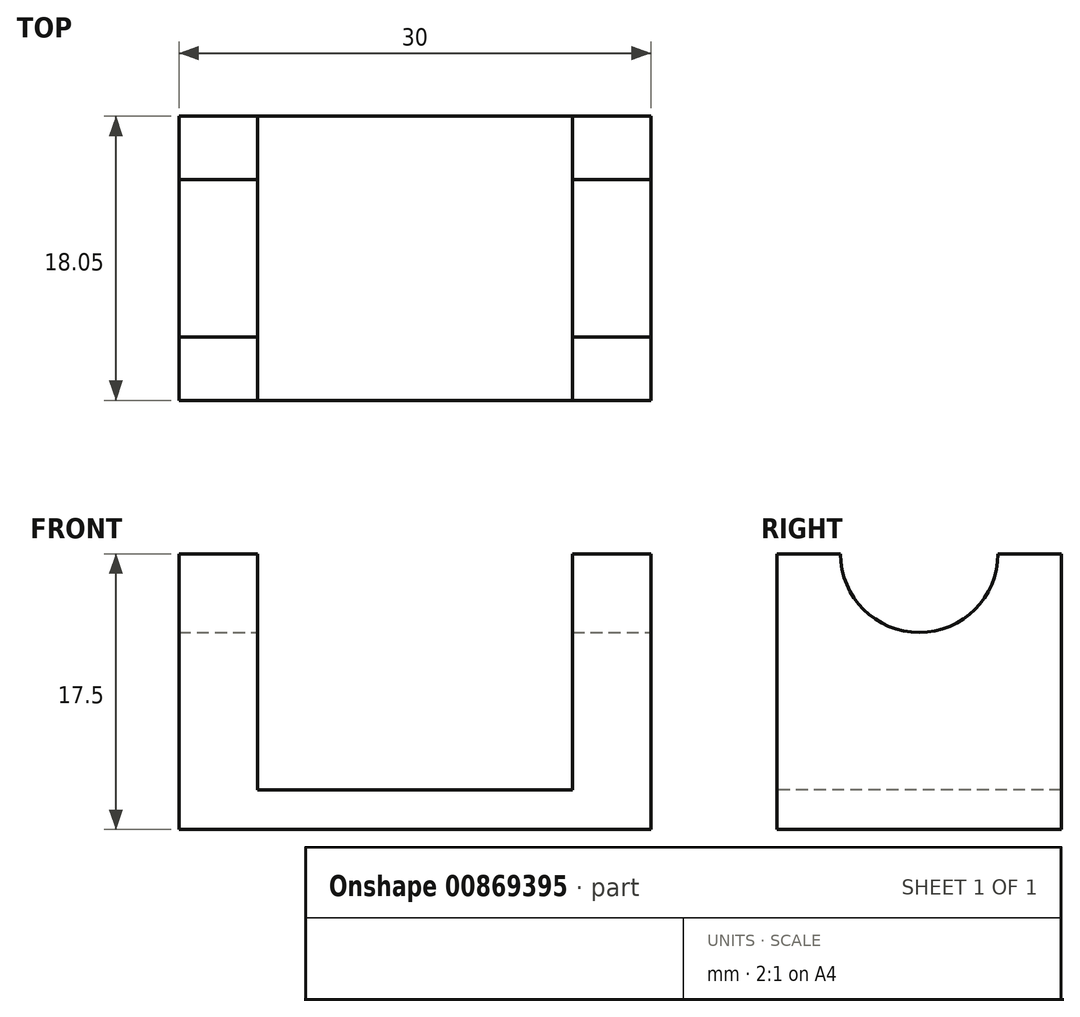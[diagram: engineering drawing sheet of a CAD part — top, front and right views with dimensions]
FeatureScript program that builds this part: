
annotation { "Feature Type Name" : "Feature", "Feature Type Description" : "" }
export const myFeature = defineFeature(function(context is Context, id is Id, definition is map)
    precondition{}
    {
        {
            var Q0;
            Q0=qCreatedBy(makeId("Top.planeOp"),FACE);
            var sketch = newSketch(context, id + "F0", { "sketchPlane" : qUnion([Q0])});
            skLineSegment(sketch, "E0.bottom", {"start": v(0, 0) * mm, "end": v(30, 0) * mm});
            skLineSegment(sketch, "E0.top", {"start": v(0, 18.05) * mm, "end": v(30, 18.05) * mm});
            skLineSegment(sketch, "E0.left", {"start": v(0, 0) * mm, "end": v(0, 18.05) * mm});
            skLineSegment(sketch, "E0.right", {"start": v(30, 0) * mm, "end": v(30, 18.05) * mm});
            skLineSegment(sketch, "E1", {"start": v(0, 9.03) * mm, "end": v(30, 9.03) * mm, "construction": true});
            skLineSegment(sketch, "E2", {"start": v(5, 18.05) * mm, "end": v(5, 0) * mm});
            skLineSegment(sketch, "E3", {"start": v(15, 9.03) * mm, "end": v(15, 0) * mm, "construction": true});
            skLineSegment(sketch, "E4.MirrorCS", {"start": v(25, 18.05) * mm, "end": v(25, 0) * mm});
            skSolve(sketch);
        }
        {
            var Q0;
            Q0 = qSketchRegion(id + "F0", true);
            extrude(context, id + "F1", {"entities" : qUnion([Q0]), "oppositeDirection" : true, "depth" : 2.5 * mm, "offsetDistance" : 25 * mm});
        }
        {
            var Q0;
            {var subQ2=sQuery(id+"F0.wireOp",EDGE,"E0.left");Q0=makeQuery(id+"F0.imprint","IMPRINT",FACE,{"disambiguationData":[TD([[makeQuery(id+"F0.imprint","IMPRINT",EDGE,{"derivedFrom":subQ2}),-1.0]])]});}
            var Q1;
            {var subQ0=sQuery(id+"F0.wireOp",EDGE,"E0.right");Q1=makeQuery(id+"F0.imprint","IMPRINT",FACE,{"disambiguationData":[TD([[makeQuery(id+"F0.imprint","IMPRINT",EDGE,{"derivedFrom":subQ0}),1.0]])]});}
            extrude(context, id + "F2", {"entities" : qUnion([Q0, Q1]), "operationType" : NewBodyOperationType.ADD, "depth" : 15 * mm, "offsetDistance" : 25 * mm});
        }
        {
            var Q0;
            {var subQ0=sQuery(id+"F0.wireOp",EDGE,"E0.right");Q0=makeQuery(id+"F2.boolean.opBoolean","MERGE",FACE,{"derivedFrom":[makeQuery(id+"F1.opExtrude","SWEPT_FACE",FACE,{"disambiguationData":[OSD([subQ0])]}),makeQuery(id+"F2.opExtrude","SWEPT_FACE",FACE,{"disambiguationData":[OSD([subQ0])]})]});}
            var sketch = newSketch(context, id + "F3", { "sketchPlane" : qUnion([Q0])});
            skCircle(sketch, "E5", {"center": v(9.03, 15) * mm, "radius": 5 * mm});
            skSolve(sketch);
        }
        {
            var Q0;
            {var subQ0=sQuery(id+"F3.wireOp",EDGE,"E5");var subQ1=makeQuery(id+"F2.opExtrude","CAP_EDGE",EDGE,{"disambiguationData":[OSD([sQuery(id+"F0.wireOp",EDGE,"E0.right")])],"isStart":false});var subQ2=makeQuery(id+"F3.imprint","INTERSECT",VERTEX,{"disambiguationData":[OD(0.0)],"derivedFrom":[subQ1,subQ0]});Q0=makeQuery(id+"F3.imprint","IMPRINT",FACE,{"disambiguationData":[TD([[makeQuery(id+"F3.imprint","IMPRINT",EDGE,{"disambiguationData":[TD([[subQ2,-1.0]])],"derivedFrom":subQ0}),1.0]])]});}
            var Q1;
            {var subQ0=sQuery(id+"F3.wireOp",EDGE,"E5");var subQ1=makeQuery(id+"F2.opExtrude","CAP_EDGE",EDGE,{"disambiguationData":[OSD([sQuery(id+"F0.wireOp",EDGE,"E0.right")])],"isStart":false});var subQ2=makeQuery(id+"F3.imprint","INTERSECT",VERTEX,{"disambiguationData":[OD(0.0)],"derivedFrom":[subQ1,subQ0]});Q1=makeQuery(id+"F3.imprint","IMPRINT",FACE,{"disambiguationData":[TD([[makeQuery(id+"F3.imprint","IMPRINT",EDGE,{"disambiguationData":[TD([[subQ2,1.0]])],"derivedFrom":subQ0}),1.0]])]});}
            extrude(context, id + "F4", {"entities" : qUnion([Q0, Q1]), "operationType" : NewBodyOperationType.REMOVE, "endBound" : BoundingType.THROUGH_ALL, "oppositeDirection" : true, "depth" : 25 * mm, "offsetDistance" : 25 * mm});
        }
    });
